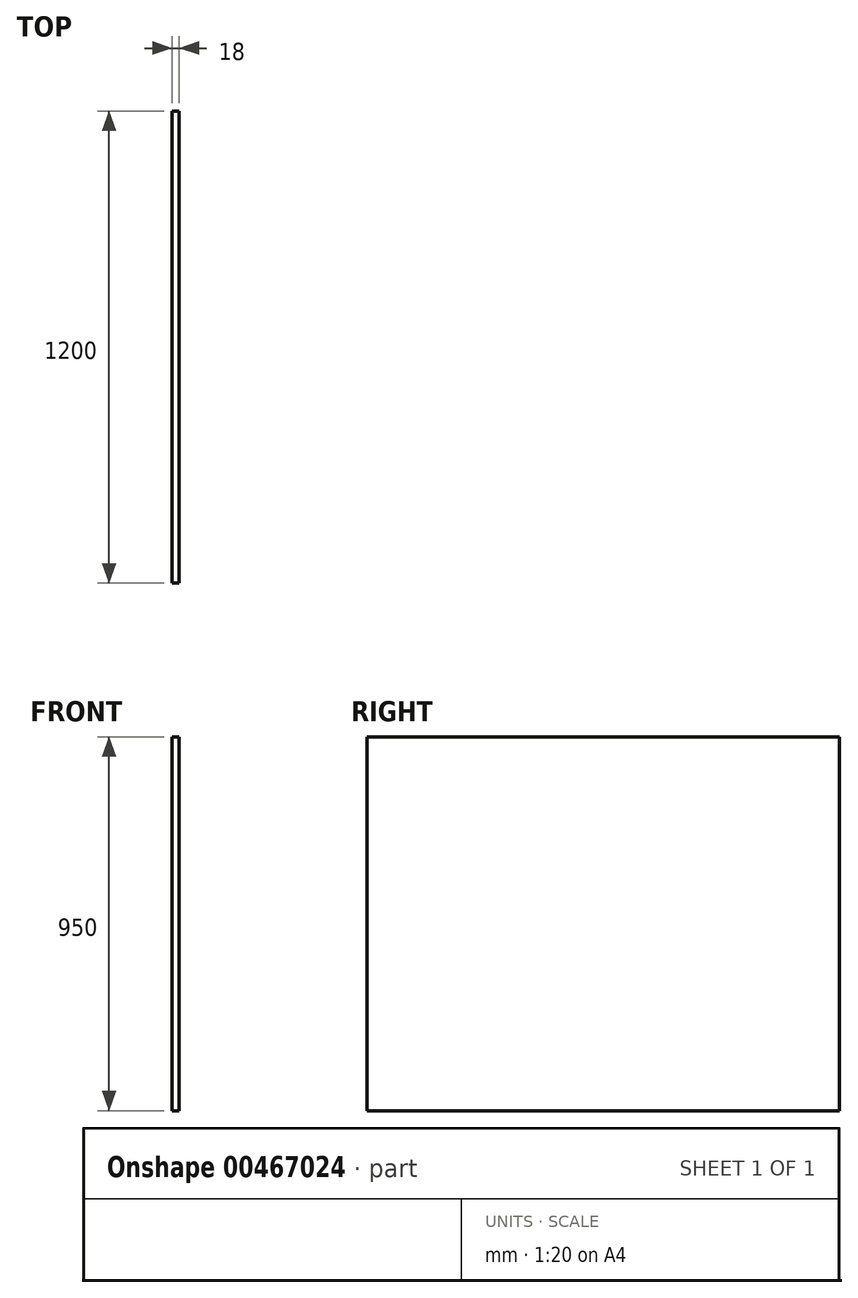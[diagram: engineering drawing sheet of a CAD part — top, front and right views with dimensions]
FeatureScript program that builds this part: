
annotation { "Feature Type Name" : "Feature", "Feature Type Description" : "" }
export const myFeature = defineFeature(function(context is Context, id is Id, definition is map)
    precondition{}
    {
        {
            var Q0;
            Q0=qCreatedBy(makeId("Right.planeOp"),FACE);
            var sketch = newSketch(context, id + "F0", { "sketchPlane" : qUnion([Q0])});
            skLineSegment(sketch, "E0.bottom", {"start": v(0, 0) * mm, "end": v(-1200, 0) * mm});
            skLineSegment(sketch, "E0.top", {"start": v(0, 950) * mm, "end": v(-1200, 950) * mm});
            skLineSegment(sketch, "E0.left", {"start": v(0, 0) * mm, "end": v(0, 950) * mm});
            skLineSegment(sketch, "E0.right", {"start": v(-1200, 0) * mm, "end": v(-1200, 950) * mm});
            skSolve(sketch);
        }
        {
            var Q0;
            Q0 = qSketchRegion(id + "F0", true);
            extrude(context, id + "F1", {"entities" : qUnion([Q0]), "oppositeDirection" : true, "depth" : 18 * mm});
        }
    });
